# Revit family: 3-5011-xx - Fugit (Vanity)
name_source: partatom
category: Lighting Fixtures
revit_build: Autodesk Revit 2017 (Build: 20160225_1515(x64)
units: mm (PartAtom-declared; Revit-internal decimal feet)

## family parameters
Cut with Voids When Loaded = No
Host = Face
Light Source = Yes
Part Type = Normal
Room Calculation Point = No
Round Connector Dimension = Use Diameter
Shared = No

## types (3) — shared parameters
2nd Diffuser = <By Category>
Color Filter = 16777215
Dimming Lamp Color Temperature Shift = <None>
Emit Shape Visible in Rendering = No
Emit from Rectangle Length = 1 "
Emit from Rectangle Width = 12 "
Lamp = LED Array
Main Diffuser = Matte White Acrylic
Manufacturer = Oxygen - Lighting & Fans
Model = 3-5011-XX - Fugit
Other 1 = <By Category>
Other 2 = <By Category>
Photometric Web File = 3-5011 Fugit.ies
Tilt Angle = 180.00°
URL = www.oxygenlighting.com
Wattage Comments = 15.0 W at 120 V
zero-valued in all types: Default Elevation

## per-type parameters (varying)
| type | Metal Finish |
| 3-5011-15 - Fugit | 15 - Black |
| 3-5011-20 - Fugit | 20 - Polished Nickel |
| 3-5011-24 - Fugit | 24 - Satin Nickel |

## geometry (parser evidence)
native form markers: Sweep x6
no freeform markers — native parametric forms only
